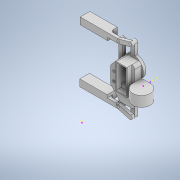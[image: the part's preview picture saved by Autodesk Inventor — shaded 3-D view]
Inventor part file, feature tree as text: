
AUTODESK INVENTOR PART (.ipt)
format: ipt  version: 2021 (Build 250183000, 183)  size: 507,392 bytes
history: native  units: mm
features: sketch x31, extrude x24, plane x22, fillet x2
ambient origin geometry x8: Origin, YZ Plane, XZ Plane, XY Plane, X Axis, Y Axis, Z Axis, Center Point
bodies: Solid1 (feature_tree)
feature tree (79):
  sketch  "Sketch1"  dims[d87=15.0mm d88=0.0mm d90=9.25mm d91=4.25mm d92=0.0mm d93=0.0mm]
  plane  "Work Plane6"
  extrude  "Extrusion19"  Depth=15.0mm TaperAngle=0.0deg
  plane  "Work Plane7"
  extrude  "Extrusion20"  Depth=10.0mm TaperAngle=0.0deg
  plane  "Work Plane8"
  extrude  "Extrusion21"  Depth=12.5mm
  plane  "Work Plane9"
  extrude  "Extrusion22"  Depth=10.0mm TaperAngle=0.0deg
  plane  "Work Plane10"
  extrude  "Extrusion23"  Depth=6.25mm
  plane  "Work Plane12"
  extrude  "Extrusion24"  Depth=3.3mm
  plane  "Work Plane11"
  extrude  "Extrusion25"  Depth=13.75mm TaperAngle=0.0deg
  plane  "Work Plane13"
  extrude  "Extrusion26"  Depth=10.0mm
  sketch  "Sketch40"  dims[d117=10.0mm d118=10.0mm]
  extrude  "Extrusion27"  Depth=10.0mm
  extrude  "Extrusion28"  Depth=10.0mm
  plane  "Work Plane15"
  extrude  "Extrusion29"  Depth=10.0mm
  sketch  "Sketch46"  dims[d125=10.0mm d126=0.0mm d134=22.5mm]
  plane  "Work Plane14"
  extrude  "Extrusion30"  Depth=10.0mm TaperAngle=0.0deg
  plane  "Work Plane16"
  extrude  "Extrusion31"  Depth=10.0mm
  plane  "Work Plane17"
  extrude  "Extrusion32"  Depth=11.25mm
  extrude  "Extrusion33"  Depth=8.0mm
  sketch  "Sketch51"  dims[d152=5.0mm d153=0.0mm d154=5.0mm d155=0.0mm]
  plane  "Work Plane22"
  extrude  "Extrusion34"  Depth=25.0mm
  plane  "Work Plane21"
  extrude  "Extrusion35"  Depth=21.25mm TaperAngle=0.0deg
  plane  "Work Plane23"
  extrude  "Extrusion36"  Depth=5.0mm TaperAngle=0.0deg
  sketch  "Sketch55"  dims[d165=3.5mm d166=26.5mm]
  plane  "Work Plane24"
  extrude  "Extrusion37"  Depth=10.0mm TaperAngle=0.0deg
  plane  "Work Plane20"
  extrude  "Extrusion38"  Depth=11.5mm
  sketch  "Sketch58"  dims[d174=1.5mm]
  plane  "Work Plane19"
  extrude  "Extrusion39"  Depth=11.5mm
  plane  "Work Plane5"
  sketch  "Sketch60"  dims[d175=1.5mm]
  plane  "Work Plane18"
  extrude  "Extrusion40"  Depth=26.5mm
  plane  "Work Plane25"
  extrude  "Extrusion41"  Depth=7.0mm
  plane  "Work Plane26"
  extrude  "Extrusion42"  Depth=1.5mm
  fillet  "Fillet3"  Radius=7.0mm
  sketch  "Sketch64"  dims[d180=5.5mm]
  fillet  "Fillet4"  Radius=1.5mm
  sketch  "Sketch65"  dims[d181=5.5mm d182=10.0mm d183=0.0mm d184=2.5mm d185=2.5mm d186=2.0mm d187=2.0mm d188=10.0mm d189=0.0mm d190=10.0mm d191=3.5mm d192=27.5mm d193=12.0mm d194=12.0mm d195=10.0mm d196=0.0mm d200=30.0mm d201=4.5mm d202=30.0mm d203=6.0mm d204=6.0mm d205=3.0mm d206=30.0mm d207=6.0mm d208=6.0mm d209=3.5mm d210=3.0mm d211=30.0mm d212=6.0mm d213=3.5mm d214=3.5mm d215=6.0mm d216=6.0mm d217=2.0mm d218=2.0mm d219=4.0mm d220=0.0mm d222=6.0mm d223=6.0mm d224=35.0mm d225=35.0mm d226=3.5mm d227=3.5mm d228=4.0mm d229=0.0mm d230=6.0mm d231=6.0mm d232=55.0mm d233=3.5mm d234=55.0mm d235=10.0mm d236=40.0mm d237=4.0mm d238=10.0mm d239=40.0mm d240=4.0mm d241=4.0mm d242=0.0mm d243=40.0mm d244=40.0mm d245=10.0mm d246=0.0mm d247=4.0mm d248=4.0mm d40=0.5mm d41=0.872665mm d42=0.5mm d43=0.872665mm d44=0.872665mm d45=0.5mm d46=0.872665mm d55=0.5mm d56=0.872665mm d57=0.5mm d58=0.872665mm d61=0.5mm d62=0.872665mm d63=0.5mm d64=0.872665mm d80=0.5mm d81=0.872665mm d82=0.5mm d83=0.872665mm d161=0.872665mm]
  sketch  "Sketch31"  dims[d94=10.0mm d95=25.0mm d96=0.0mm]
  sketch  "Sketch32"  dims[d97=12.5mm d98=12.5mm]
  sketch  "Sketch33"  dims[d99=10.0mm d100=0.0mm d103=10.0mm d104=0.0mm]
  sketch  "Sketch34"  dims[d105=5.0mm d106=6.25mm]
  sketch  "Sketch36"  dims[d107=6.25mm d108=3.3mm]
  sketch  "Sketch37"  dims[d109=3.3mm d110=13.75mm d111=0.0mm]
  sketch  "Sketch38"  dims[d112=10.0mm d113=10.0mm]
  sketch  "Sketch39"  dims[d114=10.0mm d115=0.0mm d116=22.5mm]
  sketch  "Sketch41"  dims[d119=10.0mm d120=0.0mm d121=3.5mm]
  sketch  "Sketch45"  dims[d122=3.5mm d123=10.0mm d124=0.0mm]
  sketch  "Sketch47"  dims[d143=22.5mm d144=11.25mm]
  sketch  "Sketch48"  dims[d145=8.0mm d146=8.0mm]
  sketch  "Sketch49"  dims[d147=3.5mm d148=25.0mm]
  sketch  "Sketch50"  dims[d149=3.5mm d150=21.25mm d151=0.0mm]
  sketch  "Sketch52"  dims[d156=10.0mm d157=0.0mm d158=10.0mm d159=0.0mm]
  sketch  "Sketch53"  dims[d160=5.0mm d162=11.5mm]
  sketch  "Sketch54"  dims[d163=11.5mm d164=3.5mm]
  sketch  "Sketch56"  dims[d167=10.0mm d168=0.0mm d169=7.0mm]
  sketch  "Sketch57"  dims[d170=10.0mm d171=25.0mm d172=7.0mm d173=1.5mm]
  sketch  "Sketch61"  dims[d176=19.5mm]
  sketch  "Sketch62"  dims[d177=4.5mm]
  sketch  "Sketch63"  dims[d178=7.0mm d179=0.0mm]
